# Revit family: Reece_Shower_American Standard_Cygnet_Shower Set_Twin Rail _Round
name_source: partatom
category: Plumbing Fixtures
revit_build: Autodesk Revit 2018 (Build: 20190510_1515(x64)
units: mm (PartAtom-declared; Revit-internal decimal feet)

## family parameters
Always vertical = Yes
Cut with Voids When Loaded = Yes
Part Type = Normal
Room Calculation Point = Yes
Round Connector Dimension = Use Diameter
Shared = Yes
Work Plane-Based = Yes

## types (1)
- Chrome
    Default Elevation = 0 mm  [stored 0 ft]
    Description = American Standard EasySET Thermo Controller Cygnet Round Twin Rail Shower Chrome (3 Star)
    Disclaimer = THIS FILE IS THE PROPERTY OF THE REECE GROUP. IT MAY NOT BE REPRODUCED, REVERSE-ENGINEERED OR MODIFIED. ANY REPUBLICATION, TRANSMISSION OR DISTRIBUTION FOR THE PURPOSE OF COMMERCIALLY EXPLOITING THE FILES IS PROHIBITED.
    Keynote = Product #9508982, Reece_Shower_American Standard_Cygnet_Shower Set_Twin Rail _Round - Chrome
    Manufacturer = American Standard
    Model = Cygnet
    Reece_Detail_Additional = Twin Rail Shower
    Reece_Detail_Disclaimer = THIS FILE IS THE PROPERTY OF THE REECE GROUP. IT MAY NOT BE REPRODUCED, REVERSE-ENGINEERED OR MODIFIED. ANY REPUBLICATION, TRANSMISSION OR DISTRIBUTION FOR THE PURPOSE OF COMMERCIALLY EXPLOITING THE FILES IS PROHIBITED.
    Reece_Detail_Shape = Round
    Reece_Material_Colour = Reece_Plastic_White
    Reece_Material_Main = Reece_Brass_Chrome
    Reece_Material_Secondary = Reece_Plastic_ABS
    Reece_Product_Brand = American Standard
    Reece_Product_Description = American Standard EasySET Thermo Controller Cygnet Round Twin Rail Shower Chrome (3 Star)
    Reece_Product_Mount = Wall Mounted
    Reece_Product_Number = 9508982
    Reece_Product_Sub Brand = Cygnet
    Reece_Product_Type = Shower
    Reece_Product_Web Page = https://www.reece.com.au
    Reece_Shower_Height = 1234 mm  [stored 4.04856 ft]
    Reece_Shower_Inlet = 12 mm  [stored 0.0393701 ft]
    Reece_Shower_Reach = 400 mm  [stored 1.31234 ft]
    Type Comments = Shower
    URL = https://www.reece.com.au

note: [stored X ft] marks values corroborated as IEEE doubles in the binary element streams (Revit-internal decimal feet)

## geometry (parser evidence)
native form markers: Sweep x11
no freeform markers — native parametric forms only
